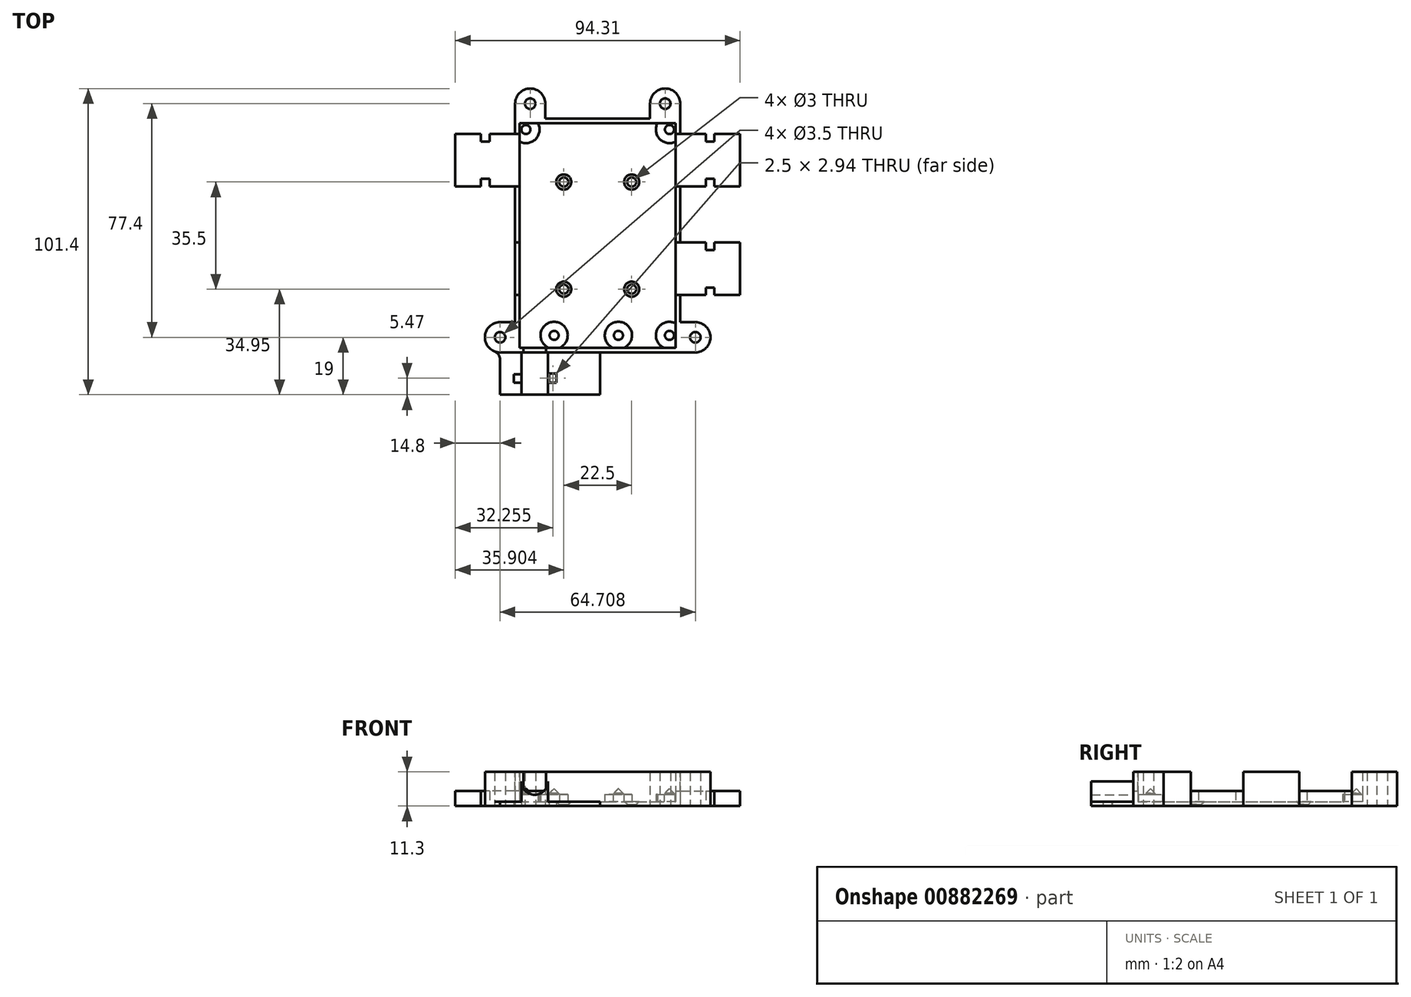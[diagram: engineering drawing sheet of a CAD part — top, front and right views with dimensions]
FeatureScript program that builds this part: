
annotation { "Feature Type Name" : "Feature", "Feature Type Description" : "" }
export const myFeature = defineFeature(function(context is Context, id is Id, definition is map)
    precondition{}
    {
        {
            var Q0;
            Q0=qCreatedBy(makeId("Top.planeOp"),FACE);
            var sketch = newSketch(context, id + "F0", { "sketchPlane" : qUnion([Q0])});
            skLineSegment(sketch, "E0.bottom", {"start": v(0, 0) * mm, "end": v(51.3, 0) * mm});
            skLineSegment(sketch, "E0.top", {"start": v(0, 74) * mm, "end": v(51.3, 74) * mm});
            skLineSegment(sketch, "E0.left", {"start": v(0, 0) * mm, "end": v(0, 74) * mm});
            skLineSegment(sketch, "E0.right", {"start": v(51.3, 0) * mm, "end": v(51.3, 74) * mm});
            skLineSegment(sketch, "E1.bottom", {"start": v(0, 69) * mm, "end": v(16.7, 69) * mm, "construction": true});
            skLineSegment(sketch, "E1.top", {"start": v(0, 55) * mm, "end": v(16.7, 55) * mm, "construction": true});
            skLineSegment(sketch, "E1.left", {"start": v(0, 69) * mm, "end": v(0, 55) * mm, "construction": true});
            skLineSegment(sketch, "E1.right", {"start": v(16.7, 69) * mm, "end": v(16.7, 55) * mm, "construction": true});
            skLineSegment(sketch, "E2.bottom", {"start": v(0, 33) * mm, "end": v(16.7, 33) * mm, "construction": true});
            skLineSegment(sketch, "E2.top", {"start": v(0, 19) * mm, "end": v(16.7, 19) * mm, "construction": true});
            skLineSegment(sketch, "E2.left", {"start": v(0, 33) * mm, "end": v(0, 19) * mm, "construction": true});
            skLineSegment(sketch, "E2.right", {"start": v(16.7, 33) * mm, "end": v(16.7, 19) * mm, "construction": true});
            skLineSegment(sketch, "E3.bottom", {"start": v(51.3, 69) * mm, "end": v(34.6, 69) * mm, "construction": true});
            skLineSegment(sketch, "E3.top", {"start": v(51.3, 55) * mm, "end": v(34.6, 55) * mm, "construction": true});
            skLineSegment(sketch, "E3.left", {"start": v(51.3, 69) * mm, "end": v(51.3, 55) * mm, "construction": true});
            skLineSegment(sketch, "E3.right", {"start": v(34.6, 69) * mm, "end": v(34.6, 55) * mm, "construction": true});
            skLineSegment(sketch, "E4.bottom", {"start": v(51.3, 33) * mm, "end": v(34.6, 33) * mm, "construction": true});
            skLineSegment(sketch, "E4.top", {"start": v(51.3, 19) * mm, "end": v(34.6, 19) * mm, "construction": true});
            skLineSegment(sketch, "E4.left", {"start": v(51.3, 33) * mm, "end": v(51.3, 19) * mm, "construction": true});
            skLineSegment(sketch, "E4.right", {"start": v(34.6, 33) * mm, "end": v(34.6, 19) * mm, "construction": true});
            skCircle(sketch, "E5", {"center": v(11.21, 3.92) * mm, "radius": 1.6 * mm});
            skCircle(sketch, "E6", {"center": v(32.51, 3.92) * mm, "radius": 1.6 * mm});
            skCircle(sketch, "E7", {"center": v(49.43, 3.92) * mm, "radius": 1.6 * mm});
            skCircle(sketch, "E8", {"center": v(49.43, 72.12) * mm, "radius": 1.6 * mm});
            skCircle(sketch, "E9", {"center": v(1.88, 72.12) * mm, "radius": 1.6 * mm});
            skLineSegment(sketch, "E10", {"start": v(1.88, 72.12) * mm, "end": v(49.43, 72.12) * mm, "construction": true});
            skSolve(sketch);
        }
        {
            var Q0;
            {var subQ10=sQuery(id+"F0.wireOp",EDGE,"E0.bottom");Q0=makeQuery(id+"F0.imprint","IMPRINT",FACE,{"disambiguationData":[TD([[makeQuery(id+"F0.imprint","IMPRINT",EDGE,{"derivedFrom":subQ10}),1.0]])]});}
            var sketch = newSketch(context, id + "F1", { "sketchPlane" : qUnion([Q0])});
            skLineSegment(sketch, "E11.0", {"start": v(-1.7, -1.7) * mm, "end": v(-1.7, 75.7) * mm});
            skLineSegment(sketch, "E11.1", {"start": v(-1.7, -1.7) * mm, "end": v(53, -1.7) * mm});
            skLineSegment(sketch, "E11.2", {"start": v(53, -1.7) * mm, "end": v(53, 75.7) * mm});
            skLineSegment(sketch, "E11.3", {"start": v(-1.7, 75.7) * mm, "end": v(53, 75.7) * mm});
            skSolve(sketch);
        }
        {
            var Q0;
            Q0=qSketchRegion(id+"F1",true);
            extrude(context, id + "F2", {"entities" : qUnion([Q0]), "depth" : 11.3 * mm, "offsetDistance" : 25 * mm});
        }
        {
            var Q0;
            Q0=makeQuery(id+"F2.opExtrude","CAP_FACE",FACE,{"disambiguationData":[OSD([sQuery(id+"F1.wireOp",EDGE,"E11.0"),sQuery(id+"F1.wireOp",EDGE,"E11.1"),sQuery(id+"F1.wireOp",EDGE,"E11.2"),sQuery(id+"F1.wireOp",EDGE,"E11.3")])],"isStart":false});
            shell(context, id + "F3", {"entities" : qUnion([Q0]), "thickness" : 1.5 * mm});
        }
        {
            var Q0;
            Q0=makeQuery(id+"F2.opExtrude","CAP_FACE",FACE,{"disambiguationData":[OSD([sQuery(id+"F1.wireOp",EDGE,"E11.0"),sQuery(id+"F1.wireOp",EDGE,"E11.1"),sQuery(id+"F1.wireOp",EDGE,"E11.2"),sQuery(id+"F1.wireOp",EDGE,"E11.3")])],"isStart":false});
            var sketch = newSketch(context, id + "F4", { "sketchPlane" : qUnion([Q0])});
            skLineSegment(sketch, "E12.0", {"start": v(16.7, 33) * mm, "end": v(16.7, 19) * mm, "construction": true});
            skLineSegment(sketch, "E13.0", {"start": v(34.6, 33) * mm, "end": v(34.6, 19) * mm, "construction": true});
            skLineSegment(sketch, "E14.0", {"start": v(16.7, 69) * mm, "end": v(16.7, 55) * mm, "construction": true});
            skLineSegment(sketch, "E15.0", {"start": v(34.6, 69) * mm, "end": v(34.6, 55) * mm, "construction": true});
            skLineSegment(sketch, "E16.0", {"start": v(0, 33) * mm, "end": v(16.7, 33) * mm, "construction": true});
            skLineSegment(sketch, "E17.0", {"start": v(0, 19) * mm, "end": v(16.7, 19) * mm, "construction": true});
            skLineSegment(sketch, "E18.0", {"start": v(51.3, 33) * mm, "end": v(34.6, 33) * mm, "construction": true});
            skLineSegment(sketch, "E19.0", {"start": v(51.3, 19) * mm, "end": v(34.6, 19) * mm, "construction": true});
            skLineSegment(sketch, "E20.0", {"start": v(51.3, 55) * mm, "end": v(34.6, 55) * mm, "construction": true});
            skLineSegment(sketch, "E21.0", {"start": v(51.3, 69) * mm, "end": v(34.6, 69) * mm, "construction": true});
            skLineSegment(sketch, "E22.0", {"start": v(0, 55) * mm, "end": v(16.7, 55) * mm, "construction": true});
            skLineSegment(sketch, "E23.0", {"start": v(0, 69) * mm, "end": v(16.7, 69) * mm, "construction": true});
            skLineSegment(sketch, "E24.0", {"start": v(0, 33) * mm, "end": v(0, 19) * mm});
            skLineSegment(sketch, "E25.0", {"start": v(51.3, 33) * mm, "end": v(51.3, 19) * mm});
            skLineSegment(sketch, "E26.0", {"start": v(0, 69) * mm, "end": v(0, 55) * mm});
            skLineSegment(sketch, "E27.0", {"start": v(51.3, 69) * mm, "end": v(51.3, 55) * mm});
            skLineSegment(sketch, "E28.0", {"start": v(-1.7, 17.3) * mm, "end": v(18.4, 17.3) * mm});
            skLineSegment(sketch, "E28.1", {"start": v(-1.7, 34.7) * mm, "end": v(-1.7, 17.3) * mm});
            skLineSegment(sketch, "E28.2", {"start": v(-1.7, 34.7) * mm, "end": v(18.4, 34.7) * mm});
            skLineSegment(sketch, "E28.3", {"start": v(18.4, 34.7) * mm, "end": v(18.4, 17.3) * mm});
            skLineSegment(sketch, "E29.0", {"start": v(53, 17.3) * mm, "end": v(32.9, 17.3) * mm});
            skLineSegment(sketch, "E29.1", {"start": v(53, 34.7) * mm, "end": v(53, 17.3) * mm});
            skLineSegment(sketch, "E29.2", {"start": v(53, 34.7) * mm, "end": v(32.9, 34.7) * mm});
            skLineSegment(sketch, "E29.3", {"start": v(32.9, 34.7) * mm, "end": v(32.9, 17.3) * mm});
            skLineSegment(sketch, "E30.0", {"start": v(-1.7, 53.3) * mm, "end": v(18.4, 53.3) * mm});
            skLineSegment(sketch, "E30.1", {"start": v(-1.7, 70.7) * mm, "end": v(-1.7, 53.3) * mm});
            skLineSegment(sketch, "E30.2", {"start": v(-1.7, 70.7) * mm, "end": v(18.4, 70.7) * mm});
            skLineSegment(sketch, "E30.3", {"start": v(18.4, 70.7) * mm, "end": v(18.4, 53.3) * mm});
            skLineSegment(sketch, "E31.0", {"start": v(53, 53.3) * mm, "end": v(32.9, 53.3) * mm});
            skLineSegment(sketch, "E31.1", {"start": v(53, 70.7) * mm, "end": v(53, 53.3) * mm});
            skLineSegment(sketch, "E31.2", {"start": v(53, 70.7) * mm, "end": v(32.9, 70.7) * mm});
            skLineSegment(sketch, "E31.3", {"start": v(32.9, 70.7) * mm, "end": v(32.9, 53.3) * mm});
            skSolve(sketch);
        }
        {
            var Q0;
            Q0=qSketchRegion(id+"F4",true);
            var Q1;
            Q1=makeQuery(id+"F3.opShell","OFFSET_FACE",FACE,{"disambiguationData":[OSD([sQuery(id+"F1.wireOp",EDGE,"E11.0"),sQuery(id+"F1.wireOp",EDGE,"E11.1"),sQuery(id+"F1.wireOp",EDGE,"E11.2"),sQuery(id+"F1.wireOp",EDGE,"E11.3")])]});
            extrude(context, id + "F5", {"entities" : qUnion([Q0]), "operationType" : NewBodyOperationType.REMOVE, "endBound" : BoundingType.UP_TO_SURFACE, "oppositeDirection" : true, "depth" : 25 * mm, "endBoundEntityFace" : qUnion([Q1]), "hasOffset" : true, "offsetDistance" : 3.5 * mm});
        }
        {
            var Q0;
            Q0=makeQuery(id+"F3.opShell","OFFSET_FACE",FACE,{"disambiguationData":[OSD([sQuery(id+"F1.wireOp",EDGE,"E11.0"),sQuery(id+"F1.wireOp",EDGE,"E11.1"),sQuery(id+"F1.wireOp",EDGE,"E11.2"),sQuery(id+"F1.wireOp",EDGE,"E11.3")])]});
            var sketch = newSketch(context, id + "F6", { "sketchPlane" : qUnion([Q0])});
            skCircle(sketch, "E32.0", {"center": v(1.88, 72.12) * mm, "radius": 1.5 * mm, "construction": true});
            skCircle(sketch, "E33.0", {"center": v(49.43, 72.12) * mm, "radius": 1.5 * mm, "construction": true});
            skCircle(sketch, "E34.0", {"center": v(11.21, 3.92) * mm, "radius": 1.5 * mm, "construction": true});
            skCircle(sketch, "E35.0", {"center": v(32.51, 3.92) * mm, "radius": 1.5 * mm, "construction": true});
            skCircle(sketch, "E36.0", {"center": v(49.43, 3.92) * mm, "radius": 1.5 * mm, "construction": true});
            skArc(sketch, "E37.0", {"start": v(-1.7, 69.4) * mm, "mid": v(6.38, 72.12) * mm, "end": v(-1.7, 74.85) * mm});
            skArc(sketch, "E38.0", {"start": v(53, 74.85) * mm, "mid": v(44.93, 72.12) * mm, "end": v(53, 69.4) * mm});
            skCircle(sketch, "E39.0", {"center": v(11.21, 3.92) * mm, "radius": 4.5 * mm});
            skCircle(sketch, "E40.0", {"center": v(32.51, 3.92) * mm, "radius": 4.5 * mm});
            skArc(sketch, "E41.0", {"start": v(53, 6.65) * mm, "mid": v(44.93, 3.92) * mm, "end": v(53, 1.2) * mm});
            skLineSegment(sketch, "E42.0", {"start": v(53, 1.2) * mm, "end": v(53, 6.65) * mm});
            skLineSegment(sketch, "E43.0", {"start": v(-1.7, 69.4) * mm, "end": v(-1.7, 74.85) * mm});
            skPoint(sketch, "E44.orphan", {"position": v(53, -1.7) * mm});
            skLineSegment(sketch, "E45.trimOffspring", {"start": v(53, 69.4) * mm, "end": v(53, 74.85) * mm});
            skPoint(sketch, "E46.orphan", {"position": v(-1.7, -1.7) * mm});
            skPoint(sketch, "E47.0.start.orphan", {"position": v(-1.7, 75.7) * mm});
            skPoint(sketch, "E48.orphan", {"position": v(53, 75.7) * mm});
            skSolve(sketch);
        }
        {
            var Q0;
            Q0=qSketchRegion(id+"F6",true);
            var Q1;
            Q1=makeQuery(id+"F5.boolean.opBoolean","COPY",FACE,{"derivedFrom":makeQuery(id+"F5.opExtrude","CAP_FACE",FACE,{"disambiguationData":[OSD([sQuery(id+"F4.wireOp",EDGE,"E28.0"),sQuery(id+"F4.wireOp",EDGE,"E28.1"),sQuery(id+"F4.wireOp",EDGE,"E28.2"),sQuery(id+"F4.wireOp",EDGE,"E28.3")])],"isStart":false})});
            extrude(context, id + "F7", {"entities" : qUnion([Q0]), "operationType" : NewBodyOperationType.ADD, "endBound" : BoundingType.UP_TO_SURFACE, "depth" : 25 * mm, "endBoundEntityFace" : qUnion([Q1]), "hasOffset" : true, "offsetDistance" : 1.2 * mm});
        }
        {
            var Q0;
            Q0=makeQuery(id+"F2.opExtrude","CAP_FACE",FACE,{"disambiguationData":[OSD([sQuery(id+"F1.wireOp",EDGE,"E11.0"),sQuery(id+"F1.wireOp",EDGE,"E11.1"),sQuery(id+"F1.wireOp",EDGE,"E11.2"),sQuery(id+"F1.wireOp",EDGE,"E11.3")])],"isStart":true});
            var sketch = newSketch(context, id + "F8", { "sketchPlane" : qUnion([Q0])});
            skLineSegment(sketch, "E49", {"start": v(25.65, -75.7) * mm, "end": v(25.65, 1.7) * mm, "construction": true});
            skLineSegment(sketch, "E50", {"start": v(-1.7, -37) * mm, "end": v(53, -37) * mm, "construction": true});
            skCircle(sketch, "E51", {"center": v(14.4, -54.75) * mm, "radius": 1.5 * mm});
            skCircle(sketch, "E52", {"center": v(14.4, -19.25) * mm, "radius": 1.5 * mm});
            skCircle(sketch, "E53", {"center": v(36.9, -19.25) * mm, "radius": 1.5 * mm});
            skCircle(sketch, "E54", {"center": v(36.9, -54.75) * mm, "radius": 1.5 * mm});
            skLineSegment(sketch, "E55", {"start": v(36.9, -54.75) * mm, "end": v(36.9, -19.25) * mm, "construction": true});
            skLineSegment(sketch, "E56", {"start": v(14.4, -19.25) * mm, "end": v(36.9, -19.25) * mm, "construction": true});
            skLineSegment(sketch, "E57", {"start": v(14.4, -54.75) * mm, "end": v(14.4, -19.25) * mm, "construction": true});
            skLineSegment(sketch, "E58", {"start": v(14.4, -54.75) * mm, "end": v(36.9, -54.75) * mm, "construction": true});
            skLineSegment(sketch, "E59", {"start": v(14.4, -37) * mm, "end": v(36.9, -37) * mm, "construction": true});
            skLineSegment(sketch, "E60", {"start": v(25.65, -19.25) * mm, "end": v(25.65, -54.75) * mm, "construction": true});
            skSolve(sketch);
        }
        {
            var Q0;
            Q0=qSketchRegion(id+"F8",true);
            extrude(context, id + "F9", {"entities" : qUnion([Q0]), "operationType" : NewBodyOperationType.REMOVE, "endBound" : BoundingType.THROUGH_ALL, "oppositeDirection" : true, "depth" : 25 * mm, "offsetDistance" : 25 * mm});
        }
        {
            var Q0;
            {var subQ0=sQuery(id+"F1.wireOp",EDGE,"E11.3");var subQ1=sQuery(id+"F1.wireOp",EDGE,"E11.2");var subQ2=sQuery(id+"F1.wireOp",EDGE,"E11.1");var subQ3=sQuery(id+"F1.wireOp",EDGE,"E11.0");Q0=makeQuery(id+"F9.boolean.opBoolean","INTERSECT",EDGE,{"derivedFrom":[makeQuery(id+"F7.boolean.opBoolean","SPLIT",FACE,{"disambiguationData":[TD([makeQuery(id+"F3.opShell","OFFSET_FACE",FACE,{"disambiguationData":[OSD([subQ3])]}),makeQuery(id+"F3.opShell","OFFSET_FACE",FACE,{"disambiguationData":[OSD([subQ2])]}),makeQuery(id+"F3.opShell","OFFSET_FACE",FACE,{"disambiguationData":[OSD([subQ1])]}),makeQuery(id+"F3.opShell","OFFSET_FACE",FACE,{"disambiguationData":[OSD([subQ0])]}),makeQuery(id+"F7.opExtrude","SWEPT_FACE",FACE,{"disambiguationData":[OSD([sQuery(id+"F6.wireOp",EDGE,"E37.0")])]}),makeQuery(id+"F7.opExtrude","SWEPT_FACE",FACE,{"disambiguationData":[OSD([sQuery(id+"F6.wireOp",EDGE,"E38.0")])]}),makeQuery(id+"F7.opExtrude","SWEPT_FACE",FACE,{"disambiguationData":[OSD([sQuery(id+"F6.wireOp",EDGE,"E39.0")])]}),makeQuery(id+"F7.opExtrude","SWEPT_FACE",FACE,{"disambiguationData":[OSD([sQuery(id+"F6.wireOp",EDGE,"E40.0")])]}),makeQuery(id+"F7.opExtrude","SWEPT_FACE",FACE,{"disambiguationData":[OSD([sQuery(id+"F6.wireOp",EDGE,"E41.0")])]})])],"derivedFrom":makeQuery(id+"F3.opShell","OFFSET_FACE",FACE,{"disambiguationData":[OSD([subQ3,subQ2,subQ1,subQ0])]})}),makeQuery(id+"F9.opExtrude","SWEPT_FACE",FACE,{"disambiguationData":[OSD([sQuery(id+"F8.wireOp",EDGE,"E54")])]})]});}
            var Q1;
            {var subQ0=sQuery(id+"F1.wireOp",EDGE,"E11.3");var subQ1=sQuery(id+"F1.wireOp",EDGE,"E11.2");var subQ2=sQuery(id+"F1.wireOp",EDGE,"E11.1");var subQ3=sQuery(id+"F1.wireOp",EDGE,"E11.0");Q1=makeQuery(id+"F9.boolean.opBoolean","INTERSECT",EDGE,{"derivedFrom":[makeQuery(id+"F7.boolean.opBoolean","SPLIT",FACE,{"disambiguationData":[TD([makeQuery(id+"F3.opShell","OFFSET_FACE",FACE,{"disambiguationData":[OSD([subQ3])]}),makeQuery(id+"F3.opShell","OFFSET_FACE",FACE,{"disambiguationData":[OSD([subQ2])]}),makeQuery(id+"F3.opShell","OFFSET_FACE",FACE,{"disambiguationData":[OSD([subQ1])]}),makeQuery(id+"F3.opShell","OFFSET_FACE",FACE,{"disambiguationData":[OSD([subQ0])]}),makeQuery(id+"F7.opExtrude","SWEPT_FACE",FACE,{"disambiguationData":[OSD([sQuery(id+"F6.wireOp",EDGE,"E37.0")])]}),makeQuery(id+"F7.opExtrude","SWEPT_FACE",FACE,{"disambiguationData":[OSD([sQuery(id+"F6.wireOp",EDGE,"E38.0")])]}),makeQuery(id+"F7.opExtrude","SWEPT_FACE",FACE,{"disambiguationData":[OSD([sQuery(id+"F6.wireOp",EDGE,"E39.0")])]}),makeQuery(id+"F7.opExtrude","SWEPT_FACE",FACE,{"disambiguationData":[OSD([sQuery(id+"F6.wireOp",EDGE,"E40.0")])]}),makeQuery(id+"F7.opExtrude","SWEPT_FACE",FACE,{"disambiguationData":[OSD([sQuery(id+"F6.wireOp",EDGE,"E41.0")])]})])],"derivedFrom":makeQuery(id+"F3.opShell","OFFSET_FACE",FACE,{"disambiguationData":[OSD([subQ3,subQ2,subQ1,subQ0])]})}),makeQuery(id+"F9.opExtrude","SWEPT_FACE",FACE,{"disambiguationData":[OSD([sQuery(id+"F8.wireOp",EDGE,"E51")])]})]});}
            var Q2;
            {var subQ0=sQuery(id+"F1.wireOp",EDGE,"E11.3");var subQ1=sQuery(id+"F1.wireOp",EDGE,"E11.2");var subQ2=sQuery(id+"F1.wireOp",EDGE,"E11.1");var subQ3=sQuery(id+"F1.wireOp",EDGE,"E11.0");Q2=makeQuery(id+"F9.boolean.opBoolean","INTERSECT",EDGE,{"derivedFrom":[makeQuery(id+"F7.boolean.opBoolean","SPLIT",FACE,{"disambiguationData":[TD([makeQuery(id+"F3.opShell","OFFSET_FACE",FACE,{"disambiguationData":[OSD([subQ3])]}),makeQuery(id+"F3.opShell","OFFSET_FACE",FACE,{"disambiguationData":[OSD([subQ2])]}),makeQuery(id+"F3.opShell","OFFSET_FACE",FACE,{"disambiguationData":[OSD([subQ1])]}),makeQuery(id+"F3.opShell","OFFSET_FACE",FACE,{"disambiguationData":[OSD([subQ0])]}),makeQuery(id+"F7.opExtrude","SWEPT_FACE",FACE,{"disambiguationData":[OSD([sQuery(id+"F6.wireOp",EDGE,"E37.0")])]}),makeQuery(id+"F7.opExtrude","SWEPT_FACE",FACE,{"disambiguationData":[OSD([sQuery(id+"F6.wireOp",EDGE,"E38.0")])]}),makeQuery(id+"F7.opExtrude","SWEPT_FACE",FACE,{"disambiguationData":[OSD([sQuery(id+"F6.wireOp",EDGE,"E39.0")])]}),makeQuery(id+"F7.opExtrude","SWEPT_FACE",FACE,{"disambiguationData":[OSD([sQuery(id+"F6.wireOp",EDGE,"E40.0")])]}),makeQuery(id+"F7.opExtrude","SWEPT_FACE",FACE,{"disambiguationData":[OSD([sQuery(id+"F6.wireOp",EDGE,"E41.0")])]})])],"derivedFrom":makeQuery(id+"F3.opShell","OFFSET_FACE",FACE,{"disambiguationData":[OSD([subQ3,subQ2,subQ1,subQ0])]})}),makeQuery(id+"F9.opExtrude","SWEPT_FACE",FACE,{"disambiguationData":[OSD([sQuery(id+"F8.wireOp",EDGE,"E53")])]})]});}
            var Q3;
            {var subQ0=sQuery(id+"F1.wireOp",EDGE,"E11.3");var subQ1=sQuery(id+"F1.wireOp",EDGE,"E11.2");var subQ2=sQuery(id+"F1.wireOp",EDGE,"E11.1");var subQ3=sQuery(id+"F1.wireOp",EDGE,"E11.0");Q3=makeQuery(id+"F9.boolean.opBoolean","INTERSECT",EDGE,{"derivedFrom":[makeQuery(id+"F7.boolean.opBoolean","SPLIT",FACE,{"disambiguationData":[TD([makeQuery(id+"F3.opShell","OFFSET_FACE",FACE,{"disambiguationData":[OSD([subQ3])]}),makeQuery(id+"F3.opShell","OFFSET_FACE",FACE,{"disambiguationData":[OSD([subQ2])]}),makeQuery(id+"F3.opShell","OFFSET_FACE",FACE,{"disambiguationData":[OSD([subQ1])]}),makeQuery(id+"F3.opShell","OFFSET_FACE",FACE,{"disambiguationData":[OSD([subQ0])]}),makeQuery(id+"F7.opExtrude","SWEPT_FACE",FACE,{"disambiguationData":[OSD([sQuery(id+"F6.wireOp",EDGE,"E37.0")])]}),makeQuery(id+"F7.opExtrude","SWEPT_FACE",FACE,{"disambiguationData":[OSD([sQuery(id+"F6.wireOp",EDGE,"E38.0")])]}),makeQuery(id+"F7.opExtrude","SWEPT_FACE",FACE,{"disambiguationData":[OSD([sQuery(id+"F6.wireOp",EDGE,"E39.0")])]}),makeQuery(id+"F7.opExtrude","SWEPT_FACE",FACE,{"disambiguationData":[OSD([sQuery(id+"F6.wireOp",EDGE,"E40.0")])]}),makeQuery(id+"F7.opExtrude","SWEPT_FACE",FACE,{"disambiguationData":[OSD([sQuery(id+"F6.wireOp",EDGE,"E41.0")])]})])],"derivedFrom":makeQuery(id+"F3.opShell","OFFSET_FACE",FACE,{"disambiguationData":[OSD([subQ3,subQ2,subQ1,subQ0])]})}),makeQuery(id+"F9.opExtrude","SWEPT_FACE",FACE,{"disambiguationData":[OSD([sQuery(id+"F8.wireOp",EDGE,"E52")])]})]});}
            chamfer(context, id + "F10", {"entities" : qUnion([Q0, Q1, Q2, Q3]), "width" : 1 * mm, "tangentPropagation" : true});
        }
        {
            var Q0;
            Q0=makeQuery(id+"F2.opExtrude","CAP_FACE",FACE,{"disambiguationData":[OSD([sQuery(id+"F1.wireOp",EDGE,"E11.0"),sQuery(id+"F1.wireOp",EDGE,"E11.1"),sQuery(id+"F1.wireOp",EDGE,"E11.2"),sQuery(id+"F1.wireOp",EDGE,"E11.3")])],"isStart":true});
            var sketch = newSketch(context, id + "F11", { "sketchPlane" : qUnion([Q0])});
            skArc(sketch, "E61", {"start": v(-6.7, 1.7) * mm, "mid": v(-11.7, -3.3) * mm, "end": v(-6.7, -8.3) * mm});
            skArc(sketch, "E62", {"start": v(-1.7, -80.7) * mm, "mid": v(3.3, -85.7) * mm, "end": v(8.3, -80.7) * mm});
            skLineSegment(sketch, "E63", {"start": v(-1.7, 1.7) * mm, "end": v(-6.7, 1.7) * mm});
            skLineSegment(sketch, "E64", {"start": v(-6.7, -8.3) * mm, "end": v(-1.7, -8.3) * mm});
            skLineSegment(sketch, "E65", {"start": v(25.65, 1.7) * mm, "end": v(25.65, -75.7) * mm, "construction": true});
            skLineSegment(sketch, "E66", {"start": v(-1.7, 1.7) * mm, "end": v(-1.7, -8.3) * mm});
            skLineSegment(sketch, "E67", {"start": v(-1.7, -75.7) * mm, "end": v(-1.7, -80.7) * mm});
            skLineSegment(sketch, "E68", {"start": v(8.3, -80.7) * mm, "end": v(8.3, -75.7) * mm});
            skLineSegment(sketch, "E69", {"start": v(-1.7, -75.7) * mm, "end": v(8.3, -75.7) * mm});
            skLineSegment(sketch, "E70.MirrorCS", {"start": v(58, -8.3) * mm, "end": v(53, -8.3) * mm});
            skLineSegment(sketch, "E71.MirrorCS", {"start": v(43, -80.7) * mm, "end": v(43, -75.7) * mm});
            skLineSegment(sketch, "E72.MirrorCS", {"start": v(53, 1.7) * mm, "end": v(58, 1.7) * mm});
            skLineSegment(sketch, "E73.MirrorCS", {"start": v(53, -75.7) * mm, "end": v(53, -80.7) * mm});
            skLineSegment(sketch, "E74.MirrorCS", {"start": v(53, 1.7) * mm, "end": v(53, -8.3) * mm});
            skLineSegment(sketch, "E75.MirrorCS", {"start": v(53, -75.7) * mm, "end": v(43, -75.7) * mm});
            skArc(sketch, "E76.MirrorCS", {"start": v(53, -80.7) * mm, "mid": v(48, -85.7) * mm, "end": v(43, -80.7) * mm});
            skArc(sketch, "E77.MirrorCS", {"start": v(58, 1.7) * mm, "mid": v(63, -3.3) * mm, "end": v(58, -8.3) * mm});
            skCircle(sketch, "E78", {"center": v(-6.7, -3.3) * mm, "radius": 1.75 * mm});
            skCircle(sketch, "E79", {"center": v(58, -3.3) * mm, "radius": 1.75 * mm});
            skCircle(sketch, "E80", {"center": v(48, -80.7) * mm, "radius": 1.75 * mm});
            skCircle(sketch, "E81", {"center": v(3.3, -80.7) * mm, "radius": 1.75 * mm});
            skSolve(sketch);
        }
        {
            var Q0;
            Q0=qSketchRegion(id+"F11",true);
            var Q1;
            {var subQ0=sQuery(id+"F1.wireOp",EDGE,"E11.0");var subQ1=sQuery(id+"F1.wireOp",EDGE,"E11.2");var subQ2=sQuery(id+"F1.wireOp",EDGE,"E11.3");Q1=makeQuery(id+"F5.boolean.opBoolean","SPLIT",FACE,{"disambiguationData":[TD([makeQuery(id+"F2.opExtrude","SWEPT_FACE",FACE,{"disambiguationData":[OSD([subQ2])]})])],"derivedFrom":makeQuery(id+"F2.opExtrude","CAP_FACE",FACE,{"disambiguationData":[OSD([subQ0,sQuery(id+"F1.wireOp",EDGE,"E11.1"),subQ1,subQ2])],"isStart":false})});}
            extrude(context, id + "F12", {"entities" : qUnion([Q0]), "operationType" : NewBodyOperationType.ADD, "endBound" : BoundingType.UP_TO_SURFACE, "oppositeDirection" : true, "depth" : 25 * mm, "endBoundEntityFace" : qUnion([Q1]), "offsetDistance" : 25 * mm});
        }
        {
            var Q0;
            Q0=makeQuery(id+"F7.opExtrude","CAP_FACE",FACE,{"disambiguationData":[OSD([sQuery(id+"F6.wireOp",EDGE,"E39.0")])],"isStart":false});
            var sketch = newSketch(context, id + "F13", { "sketchPlane" : qUnion([Q0])});
            skCircle(sketch, "E82.0", {"center": v(49.43, 3.92) * mm, "radius": 1.5 * mm});
            skCircle(sketch, "E83.0", {"center": v(32.51, 3.92) * mm, "radius": 1.5 * mm});
            skCircle(sketch, "E84.0", {"center": v(11.21, 3.92) * mm, "radius": 1.5 * mm});
            skCircle(sketch, "E85.0", {"center": v(49.43, 72.12) * mm, "radius": 1.5 * mm});
            skCircle(sketch, "E86.0", {"center": v(1.88, 72.12) * mm, "radius": 1.5 * mm});
            skSolve(sketch);
        }
        {
            var Q0;
            Q0=qSketchRegion(id+"F13",true);
            extrude(context, id + "F14", {"entities" : qUnion([Q0]), "operationType" : NewBodyOperationType.ADD, "depth" : 2 * mm, "offsetDistance" : 25 * mm});
        }
        {
            var Q0;
            Q0=makeQuery(id+"F14.opExtrude","CAP_FACE",FACE,{"disambiguationData":[OSD([sQuery(id+"F13.wireOp",EDGE,"E82.0")])],"isStart":false});
            var Q1;
            Q1=makeQuery(id+"F14.opExtrude","CAP_EDGE",EDGE,{"disambiguationData":[OSD([sQuery(id+"F13.wireOp",EDGE,"E83.0")])],"isStart":false});
            var Q2;
            Q2=makeQuery(id+"F14.opExtrude","CAP_FACE",FACE,{"disambiguationData":[OSD([sQuery(id+"F13.wireOp",EDGE,"E84.0")])],"isStart":false});
            var Q3;
            Q3=makeQuery(id+"F14.opExtrude","CAP_FACE",FACE,{"disambiguationData":[OSD([sQuery(id+"F13.wireOp",EDGE,"E85.0")])],"isStart":false});
            var Q4;
            Q4=makeQuery(id+"F14.opExtrude","CAP_EDGE",EDGE,{"disambiguationData":[OSD([sQuery(id+"F13.wireOp",EDGE,"E86.0")])],"isStart":false});
            chamfer(context, id + "F15", {"entities" : qUnion([Q0, Q1, Q2, Q3, Q4]), "width" : 1.5 * mm, "tangentPropagation" : true});
        }
        {
            var Q0;
            {var subQ0=sQuery(id+"F1.wireOp",EDGE,"E11.0");var subQ1=sQuery(id+"F1.wireOp",EDGE,"E11.2");var subQ2=sQuery(id+"F1.wireOp",EDGE,"E11.1");Q0=makeQuery(id+"F12.boolean.opBoolean","MERGE",FACE,{"derivedFrom":[makeQuery(id+"F5.boolean.opBoolean","SPLIT",FACE,{"disambiguationData":[TD([makeQuery(id+"F2.opExtrude","SWEPT_FACE",FACE,{"disambiguationData":[OSD([subQ2])]})])],"derivedFrom":makeQuery(id+"F2.opExtrude","CAP_FACE",FACE,{"disambiguationData":[OSD([subQ0,subQ2,subQ1,sQuery(id+"F1.wireOp",EDGE,"E11.3")])],"isStart":false})}),makeQuery(id+"F12.opExtrude","CAP_FACE",FACE,{"disambiguationData":[OSD([sQuery(id+"F11.wireOp",EDGE,"E61"),sQuery(id+"F11.wireOp",EDGE,"E63"),sQuery(id+"F11.wireOp",EDGE,"E64"),sQuery(id+"F11.wireOp",EDGE,"E66")])],"isStart":false}),makeQuery(id+"F12.opExtrude","CAP_FACE",FACE,{"disambiguationData":[OSD([sQuery(id+"F11.wireOp",EDGE,"E70.MirrorCS"),sQuery(id+"F11.wireOp",EDGE,"E72.MirrorCS"),sQuery(id+"F11.wireOp",EDGE,"E74.MirrorCS"),sQuery(id+"F11.wireOp",EDGE,"E77.MirrorCS")])],"isStart":false})]});}
            var sketch = newSketch(context, id + "F16", { "sketchPlane" : qUnion([Q0])});
            skLineSegment(sketch, "E87.bottom", {"start": v(1, -0.2) * mm, "end": v(8.5, -0.2) * mm});
            skLineSegment(sketch, "E87.top", {"start": v(1, -1.7) * mm, "end": v(8.5, -1.7) * mm});
            skLineSegment(sketch, "E87.left", {"start": v(1, -0.2) * mm, "end": v(1, -1.7) * mm});
            skLineSegment(sketch, "E87.right", {"start": v(8.5, -0.2) * mm, "end": v(8.5, -1.7) * mm});
            skSolve(sketch);
        }
        {
            var Q0;
            Q0=qSketchRegion(id+"F16",true);
            var Q1;
            Q1=makeQuery(id+"F5.boolean.opBoolean","COPY",FACE,{"derivedFrom":makeQuery(id+"F5.opExtrude","CAP_FACE",FACE,{"disambiguationData":[OSD([sQuery(id+"F4.wireOp",EDGE,"E28.0"),sQuery(id+"F4.wireOp",EDGE,"E28.1"),sQuery(id+"F4.wireOp",EDGE,"E28.2"),sQuery(id+"F4.wireOp",EDGE,"E28.3")])],"isStart":false})});
            extrude(context, id + "F17", {"entities" : qUnion([Q0]), "operationType" : NewBodyOperationType.REMOVE, "endBound" : BoundingType.UP_TO_SURFACE, "oppositeDirection" : true, "depth" : 25 * mm, "endBoundEntityFace" : qUnion([Q1]), "offsetDistance" : 1.2 * mm});
        }
        {
            var Q0;
            Q0=makeQuery(id+"F12.boolean.opBoolean","MERGE",FACE,{"derivedFrom":[makeQuery(id+"F2.opExtrude","CAP_FACE",FACE,{"disambiguationData":[OSD([sQuery(id+"F1.wireOp",EDGE,"E11.0"),sQuery(id+"F1.wireOp",EDGE,"E11.1"),sQuery(id+"F1.wireOp",EDGE,"E11.2"),sQuery(id+"F1.wireOp",EDGE,"E11.3")])],"isStart":true}),makeQuery(id+"F12.opExtrude","CAP_FACE",FACE,{"disambiguationData":[OSD([sQuery(id+"F11.wireOp",EDGE,"E61"),sQuery(id+"F11.wireOp",EDGE,"E63"),sQuery(id+"F11.wireOp",EDGE,"E64"),sQuery(id+"F11.wireOp",EDGE,"E66"),sQuery(id+"F11.wireOp",EDGE,"E78")])],"isStart":true}),makeQuery(id+"F12.opExtrude","CAP_FACE",FACE,{"disambiguationData":[OSD([sQuery(id+"F11.wireOp",EDGE,"E62"),sQuery(id+"F11.wireOp",EDGE,"E67"),sQuery(id+"F11.wireOp",EDGE,"E68"),sQuery(id+"F11.wireOp",EDGE,"E69"),sQuery(id+"F11.wireOp",EDGE,"E81")])],"isStart":true}),makeQuery(id+"F12.opExtrude","CAP_FACE",FACE,{"disambiguationData":[OSD([sQuery(id+"F11.wireOp",EDGE,"E70.MirrorCS"),sQuery(id+"F11.wireOp",EDGE,"E72.MirrorCS"),sQuery(id+"F11.wireOp",EDGE,"E74.MirrorCS"),sQuery(id+"F11.wireOp",EDGE,"E77.MirrorCS"),sQuery(id+"F11.wireOp",EDGE,"E79")])],"isStart":true}),makeQuery(id+"F12.opExtrude","CAP_FACE",FACE,{"disambiguationData":[OSD([sQuery(id+"F11.wireOp",EDGE,"E71.MirrorCS"),sQuery(id+"F11.wireOp",EDGE,"E73.MirrorCS"),sQuery(id+"F11.wireOp",EDGE,"E75.MirrorCS"),sQuery(id+"F11.wireOp",EDGE,"E76.MirrorCS"),sQuery(id+"F11.wireOp",EDGE,"E80")])],"isStart":true})]});
            var sketch = newSketch(context, id + "F18", { "sketchPlane" : qUnion([Q0])});
            skLineSegment(sketch, "E88.bottom", {"start": v(-1.7, -70.7) * mm, "end": v(-21.5, -70.7) * mm});
            skLineSegment(sketch, "E88.top", {"start": v(-1.7, -53.3) * mm, "end": v(-21.5, -53.3) * mm});
            skLineSegment(sketch, "E88.left", {"start": v(-1.7, -70.7) * mm, "end": v(-1.7, -53.3) * mm});
            skLineSegment(sketch, "E88.right", {"start": v(-21.5, -70.7) * mm, "end": v(-21.5, -53.3) * mm});
            skLineSegment(sketch, "E89.bottom", {"start": v(53, -70.7) * mm, "end": v(72.8, -70.7) * mm});
            skLineSegment(sketch, "E89.top", {"start": v(53, -53.3) * mm, "end": v(72.8, -53.3) * mm});
            skLineSegment(sketch, "E89.left", {"start": v(53, -70.7) * mm, "end": v(53, -53.3) * mm});
            skLineSegment(sketch, "E89.right", {"start": v(72.8, -70.7) * mm, "end": v(72.8, -53.3) * mm});
            skLineSegment(sketch, "E90.bottom", {"start": v(53, -34.7) * mm, "end": v(72.8, -34.7) * mm});
            skLineSegment(sketch, "E90.top", {"start": v(53, -17.3) * mm, "end": v(72.8, -17.3) * mm});
            skLineSegment(sketch, "E90.left", {"start": v(53, -34.7) * mm, "end": v(53, -17.3) * mm});
            skLineSegment(sketch, "E90.right", {"start": v(72.8, -34.7) * mm, "end": v(72.8, -17.3) * mm});
            skSolve(sketch);
        }
        {
            var Q0;
            Q0 = qSketchRegion(id + "F18", true);
            var Q1;
            Q1=makeQuery(id+"F5.boolean.opBoolean","COPY",FACE,{"derivedFrom":makeQuery(id+"F5.opExtrude","CAP_FACE",FACE,{"disambiguationData":[OSD([sQuery(id+"F4.wireOp",EDGE,"E30.0"),sQuery(id+"F4.wireOp",EDGE,"E30.1"),sQuery(id+"F4.wireOp",EDGE,"E30.2"),sQuery(id+"F4.wireOp",EDGE,"E30.3")])],"isStart":false})});
            extrude(context, id + "F19", {"entities" : qUnion([Q0]), "operationType" : NewBodyOperationType.ADD, "endBound" : BoundingType.UP_TO_SURFACE, "oppositeDirection" : true, "depth" : 25 * mm, "endBoundEntityFace" : qUnion([Q1]), "offsetDistance" : 25 * mm});
        }
        {
            var Q0;
            Q0=makeQuery(id+"F19.boolean.opBoolean","MERGE",FACE,{"derivedFrom":[makeQuery(id+"F12.boolean.opBoolean","MERGE",FACE,{"derivedFrom":[makeQuery(id+"F2.opExtrude","CAP_FACE",FACE,{"disambiguationData":[OSD([sQuery(id+"F1.wireOp",EDGE,"E11.0"),sQuery(id+"F1.wireOp",EDGE,"E11.1"),sQuery(id+"F1.wireOp",EDGE,"E11.2"),sQuery(id+"F1.wireOp",EDGE,"E11.3")])],"isStart":true}),makeQuery(id+"F12.opExtrude","CAP_FACE",FACE,{"disambiguationData":[OSD([sQuery(id+"F11.wireOp",EDGE,"E61"),sQuery(id+"F11.wireOp",EDGE,"E63"),sQuery(id+"F11.wireOp",EDGE,"E64"),sQuery(id+"F11.wireOp",EDGE,"E66"),sQuery(id+"F11.wireOp",EDGE,"E78")])],"isStart":true}),makeQuery(id+"F12.opExtrude","CAP_FACE",FACE,{"disambiguationData":[OSD([sQuery(id+"F11.wireOp",EDGE,"E62"),sQuery(id+"F11.wireOp",EDGE,"E67"),sQuery(id+"F11.wireOp",EDGE,"E68"),sQuery(id+"F11.wireOp",EDGE,"E69"),sQuery(id+"F11.wireOp",EDGE,"E81")])],"isStart":true}),makeQuery(id+"F12.opExtrude","CAP_FACE",FACE,{"disambiguationData":[OSD([sQuery(id+"F11.wireOp",EDGE,"E70.MirrorCS"),sQuery(id+"F11.wireOp",EDGE,"E72.MirrorCS"),sQuery(id+"F11.wireOp",EDGE,"E74.MirrorCS"),sQuery(id+"F11.wireOp",EDGE,"E77.MirrorCS"),sQuery(id+"F11.wireOp",EDGE,"E79")])],"isStart":true}),makeQuery(id+"F12.opExtrude","CAP_FACE",FACE,{"disambiguationData":[OSD([sQuery(id+"F11.wireOp",EDGE,"E71.MirrorCS"),sQuery(id+"F11.wireOp",EDGE,"E73.MirrorCS"),sQuery(id+"F11.wireOp",EDGE,"E75.MirrorCS"),sQuery(id+"F11.wireOp",EDGE,"E76.MirrorCS"),sQuery(id+"F11.wireOp",EDGE,"E80")])],"isStart":true})]}),makeQuery(id+"F19.opExtrude","CAP_FACE",FACE,{"disambiguationData":[OSD([sQuery(id+"F18.wireOp",EDGE,"E88.bottom"),sQuery(id+"F18.wireOp",EDGE,"E88.top"),sQuery(id+"F18.wireOp",EDGE,"E88.left"),sQuery(id+"F18.wireOp",EDGE,"E88.right")])],"isStart":true}),makeQuery(id+"F19.opExtrude","CAP_FACE",FACE,{"disambiguationData":[OSD([sQuery(id+"F18.wireOp",EDGE,"E89.bottom"),sQuery(id+"F18.wireOp",EDGE,"E89.top"),sQuery(id+"F18.wireOp",EDGE,"E89.left"),sQuery(id+"F18.wireOp",EDGE,"E89.right")])],"isStart":true}),makeQuery(id+"F19.opExtrude","CAP_FACE",FACE,{"disambiguationData":[OSD([sQuery(id+"F18.wireOp",EDGE,"E90.bottom"),sQuery(id+"F18.wireOp",EDGE,"E90.top"),sQuery(id+"F18.wireOp",EDGE,"E90.left"),sQuery(id+"F18.wireOp",EDGE,"E90.right")])],"isStart":true})]});
            var sketch = newSketch(context, id + "F20", { "sketchPlane" : qUnion([Q0])});
            skLineSegment(sketch, "E91.bottom", {"start": v(-6.7, 1.7) * mm, "end": v(26.5, 1.7) * mm});
            skLineSegment(sketch, "E91.top", {"start": v(-6.7, 15.7) * mm, "end": v(26.5, 15.7) * mm});
            skLineSegment(sketch, "E91.left", {"start": v(-6.7, 1.7) * mm, "end": v(-6.7, 15.7) * mm});
            skLineSegment(sketch, "E91.right", {"start": v(26.5, 1.7) * mm, "end": v(26.5, 15.7) * mm});
            skSolve(sketch);
        }
        {
            var Q0;
            Q0 = qSketchRegion(id + "F20", true);
            extrude(context, id + "F21", {"entities" : qUnion([Q0]), "operationType" : NewBodyOperationType.ADD, "oppositeDirection" : true, "depth" : 1.5 * mm, "offsetDistance" : 25 * mm});
        }
        {
            var Q0;
            Q0=makeQuery(id+"F12.boolean.opBoolean","MERGE",FACE,{"derivedFrom":[makeQuery(id+"F2.opExtrude","SWEPT_FACE",FACE,{"disambiguationData":[OSD([sQuery(id+"F1.wireOp",EDGE,"E11.1")])]}),makeQuery(id+"F12.opExtrude","SWEPT_FACE",FACE,{"disambiguationData":[OSD([sQuery(id+"F11.wireOp",EDGE,"E63")])]}),makeQuery(id+"F12.opExtrude","SWEPT_FACE",FACE,{"disambiguationData":[OSD([sQuery(id+"F11.wireOp",EDGE,"E72.MirrorCS")])]})]});
            var sketch = newSketch(context, id + "F22", { "sketchPlane" : qUnion([Q0])});
            skLineSegment(sketch, "E92", {"start": v(1, 8.15) * mm, "end": v(8.5, 8.15) * mm, "construction": true});
            skArc(sketch, "E93", {"start": v(0.35, 8.15) * mm, "mid": v(4.75, 3.75) * mm, "end": v(9.15, 8.15) * mm});
            skLineSegment(sketch, "E94", {"start": v(0.35, 1.5) * mm, "end": v(0.35, 8.15) * mm});
            skLineSegment(sketch, "E95", {"start": v(9.15, 1.5) * mm, "end": v(9.15, 8.15) * mm});
            skLineSegment(sketch, "E96", {"start": v(0.35, 1.5) * mm, "end": v(9.15, 1.5) * mm});
            skSolve(sketch);
        }
        {
            var Q0;
            Q0 = qSketchRegion(id + "F22", true);
            var Q1;
            Q1=makeQuery(id+"F21.opExtrude","SWEPT_FACE",FACE,{"disambiguationData":[OSD([sQuery(id+"F20.wireOp",EDGE,"E91.top")])]});
            extrude(context, id + "F23", {"entities" : qUnion([Q0]), "operationType" : NewBodyOperationType.ADD, "endBound" : BoundingType.UP_TO_SURFACE, "depth" : 25 * mm, "endBoundEntityFace" : qUnion([Q1]), "offsetDistance" : 25 * mm});
        }
        {
            var Q0;
            Q0=makeQuery(id+"F21.boolean.opBoolean","MERGE",FACE,{"derivedFrom":[makeQuery(id+"F19.boolean.opBoolean","MERGE",FACE,{"derivedFrom":[makeQuery(id+"F12.boolean.opBoolean","MERGE",FACE,{"derivedFrom":[makeQuery(id+"F2.opExtrude","CAP_FACE",FACE,{"disambiguationData":[OSD([sQuery(id+"F1.wireOp",EDGE,"E11.0"),sQuery(id+"F1.wireOp",EDGE,"E11.1"),sQuery(id+"F1.wireOp",EDGE,"E11.2"),sQuery(id+"F1.wireOp",EDGE,"E11.3")])],"isStart":true}),makeQuery(id+"F12.opExtrude","CAP_FACE",FACE,{"disambiguationData":[OSD([sQuery(id+"F11.wireOp",EDGE,"E61"),sQuery(id+"F11.wireOp",EDGE,"E63"),sQuery(id+"F11.wireOp",EDGE,"E64"),sQuery(id+"F11.wireOp",EDGE,"E66"),sQuery(id+"F11.wireOp",EDGE,"E78")])],"isStart":true}),makeQuery(id+"F12.opExtrude","CAP_FACE",FACE,{"disambiguationData":[OSD([sQuery(id+"F11.wireOp",EDGE,"E62"),sQuery(id+"F11.wireOp",EDGE,"E67"),sQuery(id+"F11.wireOp",EDGE,"E68"),sQuery(id+"F11.wireOp",EDGE,"E69"),sQuery(id+"F11.wireOp",EDGE,"E81")])],"isStart":true}),makeQuery(id+"F12.opExtrude","CAP_FACE",FACE,{"disambiguationData":[OSD([sQuery(id+"F11.wireOp",EDGE,"E70.MirrorCS"),sQuery(id+"F11.wireOp",EDGE,"E72.MirrorCS"),sQuery(id+"F11.wireOp",EDGE,"E74.MirrorCS"),sQuery(id+"F11.wireOp",EDGE,"E77.MirrorCS"),sQuery(id+"F11.wireOp",EDGE,"E79")])],"isStart":true}),makeQuery(id+"F12.opExtrude","CAP_FACE",FACE,{"disambiguationData":[OSD([sQuery(id+"F11.wireOp",EDGE,"E71.MirrorCS"),sQuery(id+"F11.wireOp",EDGE,"E73.MirrorCS"),sQuery(id+"F11.wireOp",EDGE,"E75.MirrorCS"),sQuery(id+"F11.wireOp",EDGE,"E76.MirrorCS"),sQuery(id+"F11.wireOp",EDGE,"E80")])],"isStart":true})]}),makeQuery(id+"F19.opExtrude","CAP_FACE",FACE,{"disambiguationData":[OSD([sQuery(id+"F18.wireOp",EDGE,"E88.bottom"),sQuery(id+"F18.wireOp",EDGE,"E88.top"),sQuery(id+"F18.wireOp",EDGE,"E88.left"),sQuery(id+"F18.wireOp",EDGE,"E88.right")])],"isStart":true}),makeQuery(id+"F19.opExtrude","CAP_FACE",FACE,{"disambiguationData":[OSD([sQuery(id+"F18.wireOp",EDGE,"E89.bottom"),sQuery(id+"F18.wireOp",EDGE,"E89.top"),sQuery(id+"F18.wireOp",EDGE,"E89.left"),sQuery(id+"F18.wireOp",EDGE,"E89.right")])],"isStart":true}),makeQuery(id+"F19.opExtrude","CAP_FACE",FACE,{"disambiguationData":[OSD([sQuery(id+"F18.wireOp",EDGE,"E90.bottom"),sQuery(id+"F18.wireOp",EDGE,"E90.top"),sQuery(id+"F18.wireOp",EDGE,"E90.left"),sQuery(id+"F18.wireOp",EDGE,"E90.right")])],"isStart":true})]}),makeQuery(id+"F21.opExtrude","CAP_FACE",FACE,{"disambiguationData":[OSD([sQuery(id+"F20.wireOp",EDGE,"E91.bottom"),sQuery(id+"F20.wireOp",EDGE,"E91.top"),sQuery(id+"F20.wireOp",EDGE,"E91.left"),sQuery(id+"F20.wireOp",EDGE,"E91.right")])],"isStart":true})]});
            var sketch = newSketch(context, id + "F24", { "sketchPlane" : qUnion([Q0])});
            skLineSegment(sketch, "E97.bottom", {"start": v(0.35, 8.9) * mm, "end": v(-2.15, 8.9) * mm});
            skLineSegment(sketch, "E97.top", {"start": v(0.35, 11.7) * mm, "end": v(-2.15, 11.7) * mm});
            skLineSegment(sketch, "E97.left", {"start": v(0.35, 8.9) * mm, "end": v(0.35, 11.7) * mm});
            skLineSegment(sketch, "E97.right", {"start": v(-2.15, 8.9) * mm, "end": v(-2.15, 11.7) * mm});
            skLineSegment(sketch, "E98.bottom", {"start": v(-13, -53.3) * mm, "end": v(-10.2, -53.3) * mm});
            skLineSegment(sketch, "E98.top", {"start": v(-13, -55.8) * mm, "end": v(-10.2, -55.8) * mm});
            skLineSegment(sketch, "E98.left", {"start": v(-13, -53.3) * mm, "end": v(-13, -55.8) * mm});
            skLineSegment(sketch, "E98.right", {"start": v(-10.2, -53.3) * mm, "end": v(-10.2, -55.8) * mm});
            skLineSegment(sketch, "E99.bottom", {"start": v(9.5, 11.7) * mm, "end": v(12, 11.7) * mm});
            skLineSegment(sketch, "E99.top", {"start": v(9.5, 8.76) * mm, "end": v(12, 8.76) * mm});
            skLineSegment(sketch, "E99.left", {"start": v(9.5, 11.7) * mm, "end": v(9.5, 8.76) * mm});
            skLineSegment(sketch, "E99.right", {"start": v(12, 11.7) * mm, "end": v(12, 8.76) * mm});
            skLineSegment(sketch, "E100", {"start": v(-11.6, -53.3) * mm, "end": v(-11.6, -70.7) * mm, "construction": true});
            skLineSegment(sketch, "E101", {"start": v(-21.5, -62) * mm, "end": v(0, -62) * mm, "construction": true});
            skLineSegment(sketch, "E102.MirrorCS", {"start": v(-13, -68.2) * mm, "end": v(-10.2, -68.2) * mm});
            skLineSegment(sketch, "E103.MirrorCS", {"start": v(-13, -70.7) * mm, "end": v(-10.2, -70.7) * mm});
            skLineSegment(sketch, "E104.MirrorCS", {"start": v(-13, -70.7) * mm, "end": v(-13, -68.2) * mm});
            skLineSegment(sketch, "E105.MirrorCS", {"start": v(-10.2, -70.7) * mm, "end": v(-10.2, -68.2) * mm});
            skLineSegment(sketch, "E106", {"start": v(25.65, -75.7) * mm, "end": v(25.65, -51.24) * mm, "construction": true});
            skLineSegment(sketch, "E107.MirrorCS", {"start": v(-10.2, -70.7) * mm, "end": v(-13, -70.7) * mm});
            skLineSegment(sketch, "E108.MirrorCS", {"start": v(-10.2, -55.8) * mm, "end": v(-13, -55.8) * mm});
            skLineSegment(sketch, "E109.MirrorCS", {"start": v(-10.2, -68.2) * mm, "end": v(-13, -68.2) * mm});
            skLineSegment(sketch, "E110.MirrorCS", {"start": v(-10.2, -53.3) * mm, "end": v(-13, -53.3) * mm});
            skLineSegment(sketch, "E111.MirrorCS", {"start": v(64.3, -70.7) * mm, "end": v(61.5, -70.7) * mm});
            skLineSegment(sketch, "E112.MirrorCS", {"start": v(64.3, -70.7) * mm, "end": v(64.3, -68.2) * mm});
            skLineSegment(sketch, "E113.MirrorCS", {"start": v(64.3, -68.2) * mm, "end": v(61.5, -68.2) * mm});
            skLineSegment(sketch, "E114.MirrorCS", {"start": v(61.5, -70.7) * mm, "end": v(61.5, -68.2) * mm});
            skLineSegment(sketch, "E115.MirrorCS", {"start": v(61.5, -68.2) * mm, "end": v(64.3, -68.2) * mm});
            skLineSegment(sketch, "E116.MirrorCS", {"start": v(61.5, -70.7) * mm, "end": v(64.3, -70.7) * mm});
            skLineSegment(sketch, "E117.MirrorCS", {"start": v(64.3, -53.3) * mm, "end": v(64.3, -55.8) * mm});
            skLineSegment(sketch, "E118.MirrorCS", {"start": v(61.5, -55.8) * mm, "end": v(64.3, -55.8) * mm});
            skLineSegment(sketch, "E119.MirrorCS", {"start": v(61.5, -53.3) * mm, "end": v(64.3, -53.3) * mm});
            skLineSegment(sketch, "E120.MirrorCS", {"start": v(61.5, -53.3) * mm, "end": v(61.5, -55.8) * mm});
            skLineSegment(sketch, "E121.MirrorCS", {"start": v(64.3, -53.3) * mm, "end": v(61.5, -53.3) * mm});
            skLineSegment(sketch, "E122.MirrorCS", {"start": v(64.3, -55.8) * mm, "end": v(61.5, -55.8) * mm});
            skLineSegment(sketch, "E123", {"start": v(53, -53.3) * mm, "end": v(53, -34.7) * mm, "construction": true});
            skLineSegment(sketch, "E124", {"start": v(53, -44) * mm, "end": v(66.37, -44) * mm, "construction": true});
            skLineSegment(sketch, "E125.MirrorCS", {"start": v(61.5, -17.3) * mm, "end": v(61.5, -19.8) * mm});
            skLineSegment(sketch, "E126.MirrorCS", {"start": v(64.3, -17.3) * mm, "end": v(64.3, -19.8) * mm});
            skLineSegment(sketch, "E127.MirrorCS", {"start": v(61.5, -34.7) * mm, "end": v(61.5, -32.2) * mm});
            skLineSegment(sketch, "E128.MirrorCS", {"start": v(64.3, -34.7) * mm, "end": v(64.3, -32.2) * mm});
            skLineSegment(sketch, "E129.MirrorCS", {"start": v(61.5, -17.3) * mm, "end": v(64.3, -17.3) * mm});
            skLineSegment(sketch, "E130.MirrorCS", {"start": v(64.3, -32.2) * mm, "end": v(61.5, -32.2) * mm});
            skLineSegment(sketch, "E131.MirrorCS", {"start": v(61.5, -34.7) * mm, "end": v(64.3, -34.7) * mm});
            skLineSegment(sketch, "E132.MirrorCS", {"start": v(64.3, -19.8) * mm, "end": v(61.5, -19.8) * mm});
            skLineSegment(sketch, "E133.MirrorCS", {"start": v(64.3, -34.7) * mm, "end": v(61.5, -34.7) * mm});
            skLineSegment(sketch, "E134.MirrorCS", {"start": v(61.5, -19.8) * mm, "end": v(64.3, -19.8) * mm});
            skLineSegment(sketch, "E135.MirrorCS", {"start": v(64.3, -17.3) * mm, "end": v(61.5, -17.3) * mm});
            skLineSegment(sketch, "E136.MirrorCS", {"start": v(61.5, -32.2) * mm, "end": v(64.3, -32.2) * mm});
            skSolve(sketch);
        }
        {
            var Q0;
            Q0 = qSketchRegion(id + "F24", true);
            extrude(context, id + "F25", {"entities" : qUnion([Q0]), "operationType" : NewBodyOperationType.REMOVE, "endBound" : BoundingType.THROUGH_ALL, "oppositeDirection" : true, "depth" : 25 * mm, "offsetDistance" : 25 * mm});
        }
        {
            var Q0;
            Q0=makeQuery(id+"F21.opExtrude","SWEPT_EDGE",EDGE,{"disambiguationData":[OSD([sQuery(id+"F1.wireOp",EDGE,"E11.1"),sQuery(id+"F11.wireOp",EDGE,"E63"),sQuery(id+"F11.wireOp",EDGE,"E72.MirrorCS"),sQuery(id+"F20.wireOp",EDGE,"E91.bottom"),sQuery(id+"F20.wireOp",EDGE,"E91.right")])]});
            var Q1;
            Q1=makeQuery(id+"F25.boolean.opBoolean","COPY",EDGE,{"derivedFrom":makeQuery(id+"F25.opExtrude","SWEPT_EDGE",EDGE,{"disambiguationData":[OSD([sQuery(id+"F18.wireOp",EDGE,"E88.top"),sQuery(id+"F24.wireOp",EDGE,"E110.MirrorCS"),sQuery(id+"F24.wireOp",EDGE,"E98.left")])]})});
            var Q2;
            Q2=makeQuery(id+"F25.boolean.opBoolean","COPY",EDGE,{"derivedFrom":makeQuery(id+"F25.opExtrude","SWEPT_EDGE",EDGE,{"disambiguationData":[OSD([sQuery(id+"F18.wireOp",EDGE,"E88.top"),sQuery(id+"F24.wireOp",EDGE,"E110.MirrorCS"),sQuery(id+"F24.wireOp",EDGE,"E98.right")])]})});
            var Q3;
            Q3=makeQuery(id+"F25.boolean.opBoolean","COPY",EDGE,{"derivedFrom":makeQuery(id+"F25.opExtrude","SWEPT_EDGE",EDGE,{"disambiguationData":[OSD([sQuery(id+"F18.wireOp",EDGE,"E90.top"),sQuery(id+"F24.wireOp",EDGE,"E125.MirrorCS"),sQuery(id+"F24.wireOp",EDGE,"E135.MirrorCS")])]})});
            var Q4;
            Q4=makeQuery(id+"F25.boolean.opBoolean","COPY",EDGE,{"derivedFrom":makeQuery(id+"F25.opExtrude","SWEPT_EDGE",EDGE,{"disambiguationData":[OSD([sQuery(id+"F18.wireOp",EDGE,"E90.top"),sQuery(id+"F24.wireOp",EDGE,"E126.MirrorCS"),sQuery(id+"F24.wireOp",EDGE,"E135.MirrorCS")])]})});
            var Q5;
            Q5=makeQuery(id+"F25.boolean.opBoolean","COPY",EDGE,{"derivedFrom":makeQuery(id+"F25.opExtrude","SWEPT_EDGE",EDGE,{"disambiguationData":[OSD([sQuery(id+"F18.wireOp",EDGE,"E90.bottom"),sQuery(id+"F24.wireOp",EDGE,"E127.MirrorCS"),sQuery(id+"F24.wireOp",EDGE,"E133.MirrorCS")])]})});
            var Q6;
            Q6=makeQuery(id+"F25.boolean.opBoolean","COPY",EDGE,{"derivedFrom":makeQuery(id+"F25.opExtrude","SWEPT_EDGE",EDGE,{"disambiguationData":[OSD([sQuery(id+"F18.wireOp",EDGE,"E90.bottom"),sQuery(id+"F24.wireOp",EDGE,"E128.MirrorCS"),sQuery(id+"F24.wireOp",EDGE,"E133.MirrorCS")])]})});
            var Q7;
            Q7=makeQuery(id+"F25.boolean.opBoolean","COPY",EDGE,{"derivedFrom":makeQuery(id+"F25.opExtrude","SWEPT_EDGE",EDGE,{"disambiguationData":[OSD([sQuery(id+"F18.wireOp",EDGE,"E89.top"),sQuery(id+"F24.wireOp",EDGE,"E117.MirrorCS"),sQuery(id+"F24.wireOp",EDGE,"E121.MirrorCS")])]})});
            var Q8;
            Q8=makeQuery(id+"F25.boolean.opBoolean","COPY",EDGE,{"derivedFrom":makeQuery(id+"F25.opExtrude","SWEPT_EDGE",EDGE,{"disambiguationData":[OSD([sQuery(id+"F18.wireOp",EDGE,"E89.bottom"),sQuery(id+"F24.wireOp",EDGE,"E111.MirrorCS"),sQuery(id+"F24.wireOp",EDGE,"E112.MirrorCS")])]})});
            var Q9;
            Q9=makeQuery(id+"F25.boolean.opBoolean","COPY",EDGE,{"derivedFrom":makeQuery(id+"F25.opExtrude","SWEPT_EDGE",EDGE,{"disambiguationData":[OSD([sQuery(id+"F18.wireOp",EDGE,"E89.top"),sQuery(id+"F24.wireOp",EDGE,"E120.MirrorCS"),sQuery(id+"F24.wireOp",EDGE,"E121.MirrorCS")])]})});
            var Q10;
            Q10=makeQuery(id+"F25.boolean.opBoolean","COPY",EDGE,{"derivedFrom":makeQuery(id+"F25.opExtrude","SWEPT_EDGE",EDGE,{"disambiguationData":[OSD([sQuery(id+"F18.wireOp",EDGE,"E89.bottom"),sQuery(id+"F24.wireOp",EDGE,"E114.MirrorCS"),sQuery(id+"F24.wireOp",EDGE,"E111.MirrorCS")])]})});
            var Q11;
            Q11=makeQuery(id+"F19.opExtrude","SWEPT_EDGE",EDGE,{"disambiguationData":[OSD([sQuery(id+"F1.wireOp",EDGE,"E11.2"),sQuery(id+"F11.wireOp",EDGE,"E73.MirrorCS"),sQuery(id+"F18.wireOp",EDGE,"E89.top"),sQuery(id+"F18.wireOp",EDGE,"E89.left")])]});
            var Q12;
            Q12=makeQuery(id+"F19.opExtrude","SWEPT_EDGE",EDGE,{"disambiguationData":[OSD([sQuery(id+"F1.wireOp",EDGE,"E11.2"),sQuery(id+"F11.wireOp",EDGE,"E73.MirrorCS"),sQuery(id+"F18.wireOp",EDGE,"E90.bottom"),sQuery(id+"F18.wireOp",EDGE,"E90.left")])]});
            var Q13;
            Q13=makeQuery(id+"F19.opExtrude","SWEPT_EDGE",EDGE,{"disambiguationData":[OSD([sQuery(id+"F1.wireOp",EDGE,"E11.2"),sQuery(id+"F11.wireOp",EDGE,"E73.MirrorCS"),sQuery(id+"F18.wireOp",EDGE,"E89.bottom"),sQuery(id+"F18.wireOp",EDGE,"E89.left")])]});
            var Q14;
            Q14=makeQuery(id+"F19.opExtrude","SWEPT_EDGE",EDGE,{"disambiguationData":[OSD([sQuery(id+"F1.wireOp",EDGE,"E11.0"),sQuery(id+"F11.wireOp",EDGE,"E67"),sQuery(id+"F18.wireOp",EDGE,"E88.top"),sQuery(id+"F18.wireOp",EDGE,"E88.left")])]});
            var Q15;
            Q15=makeQuery(id+"F19.opExtrude","SWEPT_EDGE",EDGE,{"disambiguationData":[OSD([sQuery(id+"F1.wireOp",EDGE,"E11.0"),sQuery(id+"F11.wireOp",EDGE,"E67"),sQuery(id+"F18.wireOp",EDGE,"E88.bottom"),sQuery(id+"F18.wireOp",EDGE,"E88.left")])]});
            var Q16;
            Q16=makeQuery(id+"F25.boolean.opBoolean","COPY",EDGE,{"derivedFrom":makeQuery(id+"F25.opExtrude","SWEPT_EDGE",EDGE,{"disambiguationData":[OSD([sQuery(id+"F18.wireOp",EDGE,"E88.bottom"),sQuery(id+"F24.wireOp",EDGE,"E103.MirrorCS"),sQuery(id+"F24.wireOp",EDGE,"E105.MirrorCS")])]})});
            var Q17;
            Q17=makeQuery(id+"F25.boolean.opBoolean","COPY",EDGE,{"derivedFrom":makeQuery(id+"F25.opExtrude","SWEPT_EDGE",EDGE,{"disambiguationData":[OSD([sQuery(id+"F18.wireOp",EDGE,"E88.bottom"),sQuery(id+"F24.wireOp",EDGE,"E103.MirrorCS"),sQuery(id+"F24.wireOp",EDGE,"E104.MirrorCS")])]})});
            var Q18;
            {var subQ0=sQuery(id+"F11.wireOp",EDGE,"E61");Q18=makeQuery(id+"F21.boolean.opBoolean","MERGE",EDGE,{"derivedFrom":[makeQuery(id+"F12.opExtrude","SWEPT_EDGE",EDGE,{"disambiguationData":[OSD([subQ0,sQuery(id+"F11.wireOp",EDGE,"E63")])]}),makeQuery(id+"F21.opExtrude","SWEPT_EDGE",EDGE,{"disambiguationData":[OSD([subQ0,sQuery(id+"F20.wireOp",EDGE,"E91.bottom"),sQuery(id+"F20.wireOp",EDGE,"E91.left")])]})]});}
            fillet(context, id + "F26", {"entities" : qUnion([Q0, Q1, Q2, Q3, Q4, Q5, Q6, Q7, Q8, Q9, Q10, Q11, Q12, Q13, Q14, Q15, Q16, Q17, Q18]), "radius" : 2.9 * mm, "tangentPropagation" : true, "allowEdgeOverflow" : false});
        }
    });
